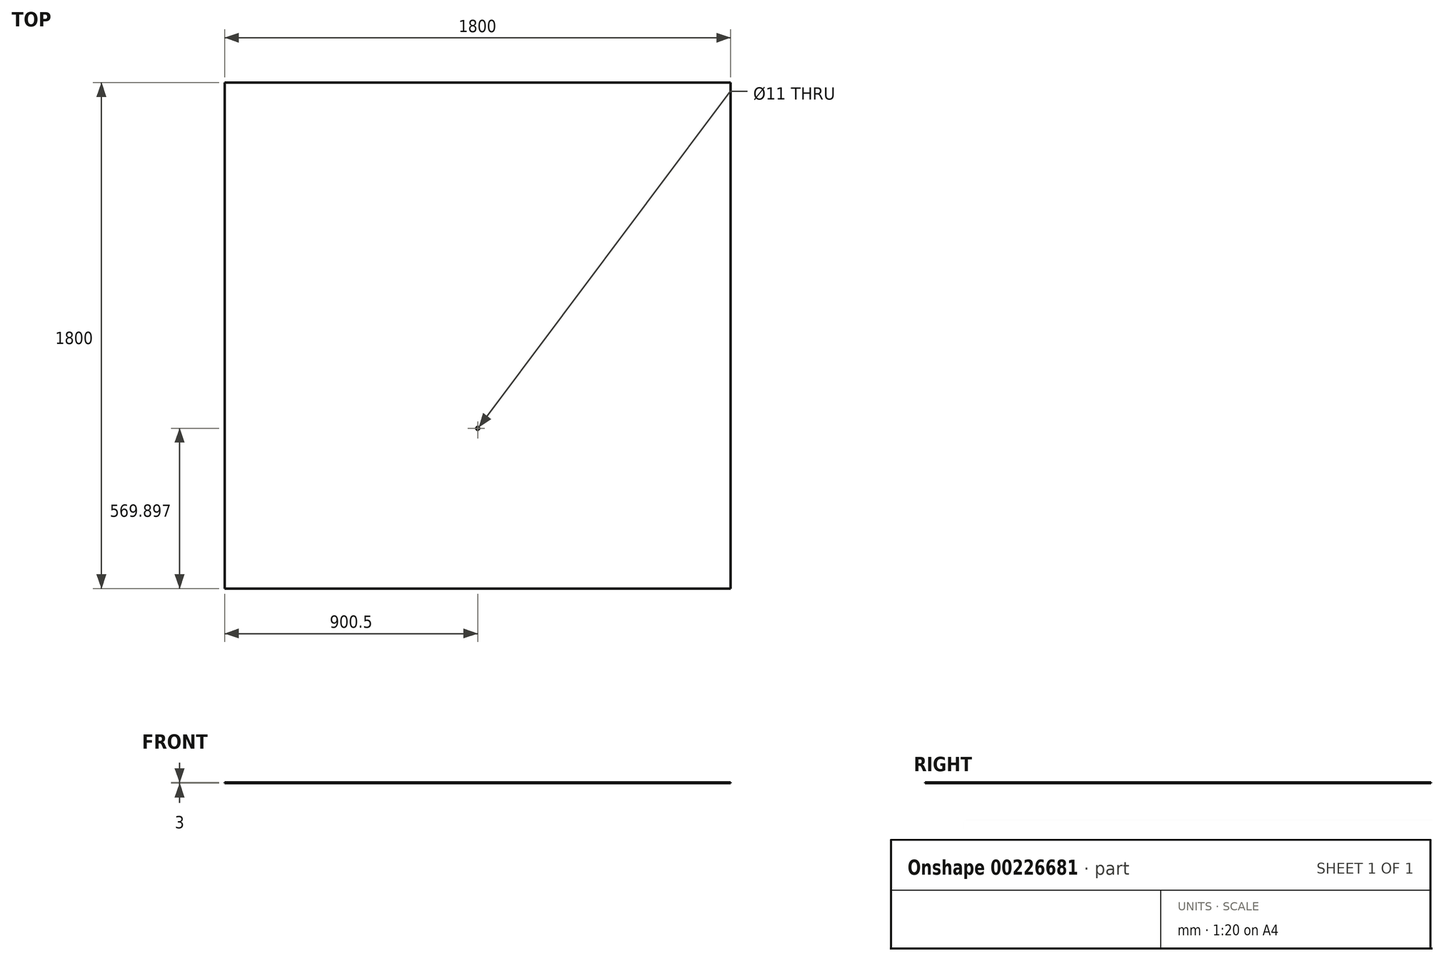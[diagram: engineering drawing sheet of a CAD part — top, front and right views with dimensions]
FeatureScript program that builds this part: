
annotation { "Feature Type Name" : "Feature", "Feature Type Description" : "" }
export const myFeature = defineFeature(function(context is Context, id is Id, definition is map)
    precondition{}
    {
        {
            var Q0;
            Q0=qCreatedBy(makeId("Top.planeOp"),FACE);
            var sketch = newSketch(context, id + "F0", { "sketchPlane" : qUnion([Q0])});
            skLineSegment(sketch, "E0.bottom", {"start": v(900, -900) * mm, "end": v(-900, -900) * mm});
            skLineSegment(sketch, "E0.top", {"start": v(900, 900) * mm, "end": v(-900, 900) * mm});
            skLineSegment(sketch, "E0.left", {"start": v(900, -900) * mm, "end": v(900, 900) * mm});
            skLineSegment(sketch, "E0.right", {"start": v(-900, -900) * mm, "end": v(-900, 900) * mm});
            skPoint(sketch, "E0.middle", {"position": v(0, 0) * mm});
            skLineSegment(sketch, "E1", {"start": v(900, -900) * mm, "end": v(0.5, -900) * mm});
            skLineSegment(sketch, "E2", {"start": v(0.5, -900) * mm, "end": v(0.5, -330.1) * mm});
            skCircle(sketch, "E3", {"center": v(0.5, -330.1) * mm, "radius": 5.5 * mm});
            skSolve(sketch);
        }
        {
            var Q0;
            Q0=makeQuery(id+"F0.imprint","IMPRINT",FACE,{"disambiguationData":[TD([[makeQuery(id+"F0.imprint","IMPRINT",EDGE,{"derivedFrom":sQuery(id+"F0.wireOp",EDGE,"E0.bottom")}),-1.0]])]});
            extrude(context, id + "F1", {"entities" : qUnion([Q0]), "depth" : 3 * mm});
        }
    });
